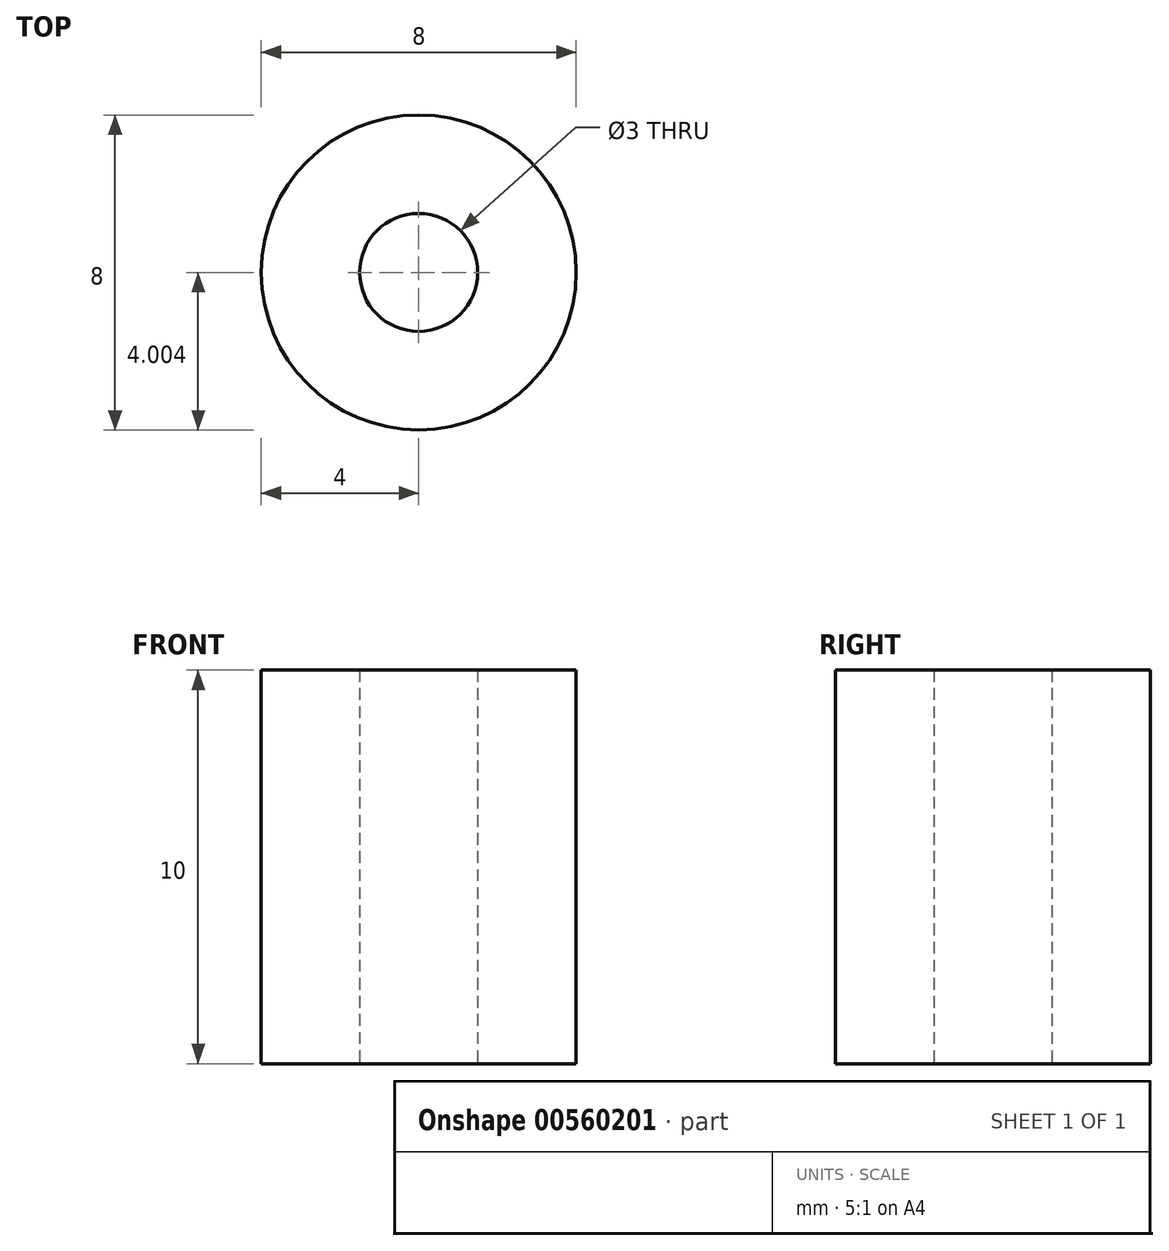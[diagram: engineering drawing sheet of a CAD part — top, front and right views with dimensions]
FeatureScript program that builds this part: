
annotation { "Feature Type Name" : "Feature", "Feature Type Description" : "" }
export const myFeature = defineFeature(function(context is Context, id is Id, definition is map)
    precondition{}
    {
        {
            var Q0;
            Q0=qCreatedBy(makeId("Top.planeOp"),FACE);
            var sketch = newSketch(context, id + "F0", { "sketchPlane" : qUnion([Q0])});
            skCircle(sketch, "E0", {"center": v(0, 1.26) * mm, "radius": 4 * mm});
            skCircle(sketch, "E1", {"center": v(0, 1.26) * mm, "radius": 1.5 * mm});
            skSolve(sketch);
        }
        {
            var Q0;
            Q0=makeQuery(id+"F0.imprint","IMPRINT",FACE,{"disambiguationData":[TD([[makeQuery(id+"F0.imprint","IMPRINT",EDGE,{"derivedFrom":sQuery(id+"F0.wireOp",EDGE,"E0")}),1.0]])]});
            extrude(context, id + "F1", {"entities" : qUnion([Q0]), "depth" : 10 * mm, "offsetDistance" : 25 * mm});
        }
    });
